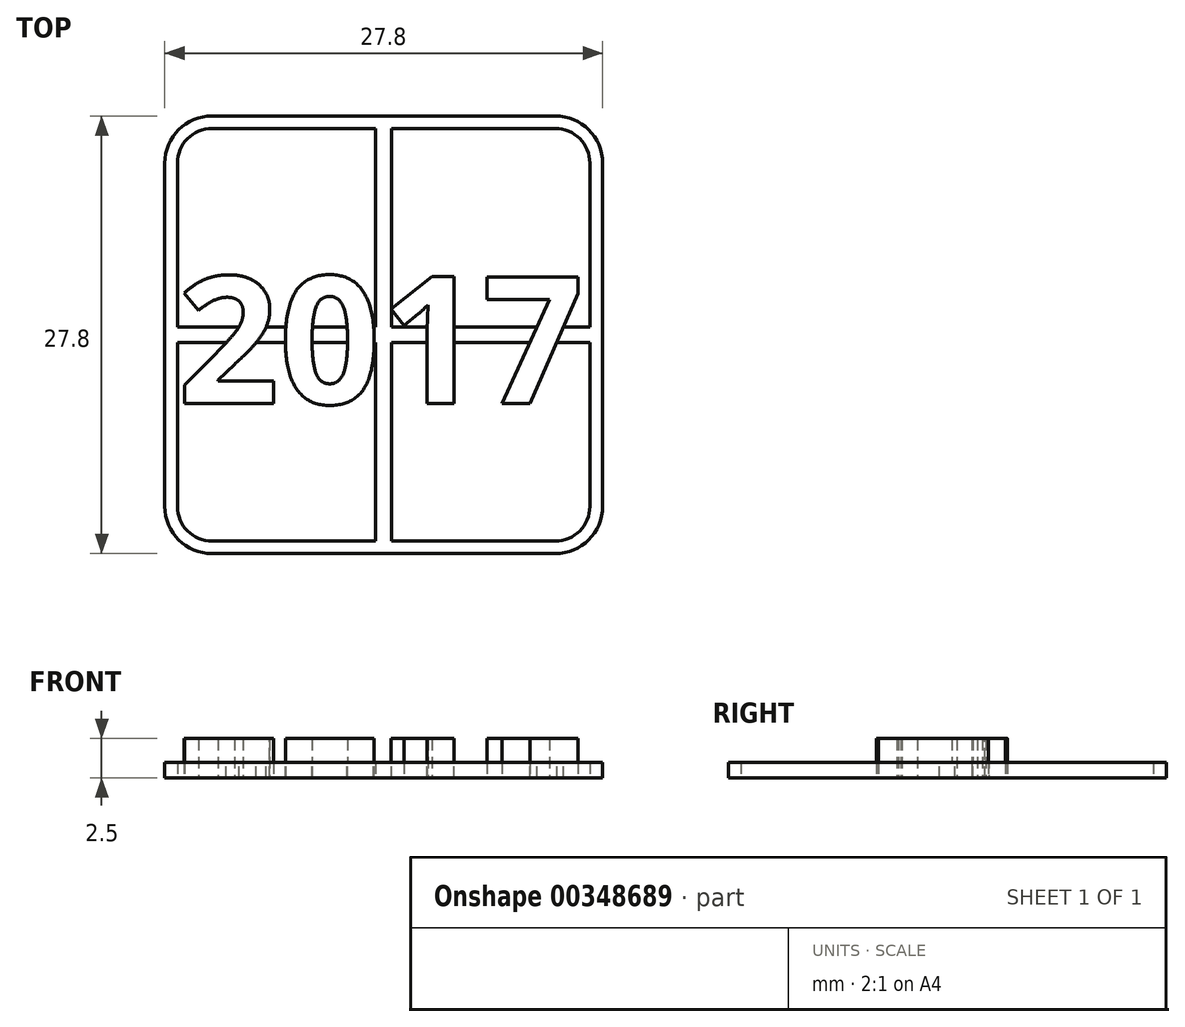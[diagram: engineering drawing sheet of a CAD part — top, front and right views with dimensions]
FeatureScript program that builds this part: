
annotation { "Feature Type Name" : "Feature", "Feature Type Description" : "" }
export const myFeature = defineFeature(function(context is Context, id is Id, definition is map)
    precondition{}
    {
        {
            var Q0;
            Q0=qCreatedBy(makeId("Top.planeOp"),FACE);
            var sketch = newSketch(context, id + "F0", { "sketchPlane" : qUnion([Q0])});
            skLineSegment(sketch, "E0", {"start": v(-13.9, 10.9) * mm, "end": v(-13.9, -10.9) * mm});
            skLineSegment(sketch, "E1", {"start": v(13.9, -10.9) * mm, "end": v(13.9, 10.9) * mm});
            skLineSegment(sketch, "E2", {"start": v(-10.9, 13.9) * mm, "end": v(10.9, 13.9) * mm});
            skLineSegment(sketch, "E3", {"start": v(-10.9, -13.9) * mm, "end": v(10.9, -13.9) * mm});
            skLineSegment(sketch, "E4", {"start": v(0, 13.9) * mm, "end": v(0, -13.9) * mm, "construction": true});
            skLineSegment(sketch, "E5", {"start": v(-13.9, 0) * mm, "end": v(13.9, 0) * mm, "construction": true});
            skPoint(sketch, "E6", {"position": v(0, 0) * mm});
            skPoint(sketch, "E7", {"position": v(0, 13.9) * mm});
            skPoint(sketch, "E8", {"position": v(0, -13.9) * mm});
            skPoint(sketch, "E9", {"position": v(-13.9, 0) * mm});
            skPoint(sketch, "E10", {"position": v(13.9, 0) * mm});
            skArc(sketch, "E11", {"start": v(-10.9, 13.9) * mm, "mid": v(-13.02, 13.02) * mm, "end": v(-13.9, 10.9) * mm});
            skArc(sketch, "E12", {"start": v(13.9, 10.9) * mm, "mid": v(13.02, 13.02) * mm, "end": v(10.9, 13.9) * mm});
            skArc(sketch, "E13", {"start": v(-13.9, -10.9) * mm, "mid": v(-13.02, -13.02) * mm, "end": v(-10.9, -13.9) * mm});
            skArc(sketch, "E14", {"start": v(10.9, -13.9) * mm, "mid": v(13.02, -13.02) * mm, "end": v(13.9, -10.9) * mm});
            skLineSegment(sketch, "E15", {"start": v(-0.5, 13.1) * mm, "end": v(-0.5, 0.5) * mm});
            skLineSegment(sketch, "E16", {"start": v(-0.5, 0.5) * mm, "end": v(-13.1, 0.5) * mm});
            skLineSegment(sketch, "E17", {"start": v(-13.1, 0.5) * mm, "end": v(-13.1, 10.9) * mm});
            skLineSegment(sketch, "E18", {"start": v(-0.5, 13.1) * mm, "end": v(-10.9, 13.1) * mm});
            skArc(sketch, "E19", {"start": v(-10.9, 13.1) * mm, "mid": v(-12.46, 12.46) * mm, "end": v(-13.1, 10.9) * mm});
            skLineSegment(sketch, "E20.MirrorCS", {"start": v(13.1, 0.5) * mm, "end": v(13.1, 10.9) * mm});
            skLineSegment(sketch, "E21.MirrorCS", {"start": v(0.5, 0.5) * mm, "end": v(13.1, 0.5) * mm});
            skLineSegment(sketch, "E22.MirrorCS", {"start": v(0.5, 13.1) * mm, "end": v(10.9, 13.1) * mm});
            skLineSegment(sketch, "E23.MirrorCS", {"start": v(0.5, 13.1) * mm, "end": v(0.5, 0.5) * mm});
            skArc(sketch, "E24.MirrorCS", {"start": v(10.9, 13.1) * mm, "mid": v(12.46, 12.46) * mm, "end": v(13.1, 10.9) * mm});
            skLineSegment(sketch, "E25.MirrorCS", {"start": v(0.5, -13.1) * mm, "end": v(10.9, -13.1) * mm});
            skLineSegment(sketch, "E26.MirrorCS", {"start": v(13.1, -0.5) * mm, "end": v(13.1, -10.9) * mm});
            skArc(sketch, "E27.MirrorCS", {"start": v(10.9, -13.1) * mm, "mid": v(12.46, -12.46) * mm, "end": v(13.1, -10.9) * mm});
            skLineSegment(sketch, "E28.MirrorCS", {"start": v(0.5, -13.1) * mm, "end": v(0.5, -0.5) * mm});
            skLineSegment(sketch, "E29.MirrorCS", {"start": v(0.5, -0.5) * mm, "end": v(13.1, -0.5) * mm});
            skLineSegment(sketch, "E30.MirrorCS", {"start": v(-0.5, -0.5) * mm, "end": v(-13.1, -0.5) * mm});
            skLineSegment(sketch, "E31.MirrorCS", {"start": v(-0.5, -13.1) * mm, "end": v(-0.5, -0.5) * mm});
            skLineSegment(sketch, "E32.MirrorCS", {"start": v(-0.5, -13.1) * mm, "end": v(-10.9, -13.1) * mm});
            skLineSegment(sketch, "E33.MirrorCS", {"start": v(-13.1, -0.5) * mm, "end": v(-13.1, -10.9) * mm});
            skArc(sketch, "E34.MirrorCS", {"start": v(-10.9, -13.1) * mm, "mid": v(-12.46, -12.46) * mm, "end": v(-13.1, -10.9) * mm});
            skSolve(sketch);
        }
        {
            var Q0;
            Q0=makeQuery(id+"F0.imprint","IMPRINT",FACE,{"disambiguationData":[TD([[makeQuery(id+"F0.imprint","IMPRINT",EDGE,{"derivedFrom":sQuery(id+"F0.wireOp",EDGE,"E0")}),1.0]])]});
            extrude(context, id + "F1", {"entities" : qUnion([Q0]), "depth" : 1 * mm});
        }
        {
            var Q0;
            Q0=makeQuery(id+"F1.opExtrude","CAP_FACE",FACE,{"disambiguationData":[OSD([sQuery(id+"F0.wireOp",EDGE,"E0"),sQuery(id+"F0.wireOp",EDGE,"E1"),sQuery(id+"F0.wireOp",EDGE,"E2"),sQuery(id+"F0.wireOp",EDGE,"E3"),sQuery(id+"F0.wireOp",EDGE,"E11"),sQuery(id+"F0.wireOp",EDGE,"E12"),sQuery(id+"F0.wireOp",EDGE,"E13"),sQuery(id+"F0.wireOp",EDGE,"E14"),sQuery(id+"F0.wireOp",EDGE,"E15"),sQuery(id+"F0.wireOp",EDGE,"E16"),sQuery(id+"F0.wireOp",EDGE,"E17"),sQuery(id+"F0.wireOp",EDGE,"E18"),sQuery(id+"F0.wireOp",EDGE,"E19"),sQuery(id+"F0.wireOp",EDGE,"E20.MirrorCS"),sQuery(id+"F0.wireOp",EDGE,"E21.MirrorCS"),sQuery(id+"F0.wireOp",EDGE,"E22.MirrorCS"),sQuery(id+"F0.wireOp",EDGE,"E23.MirrorCS"),sQuery(id+"F0.wireOp",EDGE,"E24.MirrorCS"),sQuery(id+"F0.wireOp",EDGE,"E25.MirrorCS"),sQuery(id+"F0.wireOp",EDGE,"E26.MirrorCS"),sQuery(id+"F0.wireOp",EDGE,"E27.MirrorCS"),sQuery(id+"F0.wireOp",EDGE,"E28.MirrorCS"),sQuery(id+"F0.wireOp",EDGE,"E29.MirrorCS"),sQuery(id+"F0.wireOp",EDGE,"E30.MirrorCS"),sQuery(id+"F0.wireOp",EDGE,"E31.MirrorCS"),sQuery(id+"F0.wireOp",EDGE,"E32.MirrorCS"),sQuery(id+"F0.wireOp",EDGE,"E33.MirrorCS"),sQuery(id+"F0.wireOp",EDGE,"E34.MirrorCS")])],"isStart":false});
            var sketch = newSketch(context, id + "F2", { "sketchPlane" : qUnion([Q0])});
            skText(sketch, "E35", { "text": "2017", "fontName": "OpenSans-Bold.ttf"});
            const initialGuessF2  = {"E35": [-0.0131, -0.00438, 1, 0, 0.00814]};
            skSetInitialGuess(sketch, initialGuessF2);
            skSolve(sketch);
        }
        {
            var Q0;
            Q0 = qSketchRegion(id + "F2", true);
            extrude(context, id + "F3", {"entities" : qUnion([Q0]), "operationType" : NewBodyOperationType.ADD, "depth" : 1.5 * mm});
        }
        {
            var Q0;
            {var subQ0=sQuery(id+"F2.wireOp",EDGE,"E35.sketch_text.stroke-50");var subQ2=sQuery(id+"F2.wireOp",EDGE,"E35.sketch_text.stroke-51");var subQ3=sQuery(id+"F2.wireOp",EDGE,"E35.sketch_text.stroke-52");var subQ4=sQuery(id+"F2.wireOp",EDGE,"E35.sketch_text.stroke-53");var subQ5=sQuery(id+"F2.wireOp",EDGE,"E35.sketch_text.stroke-54");var subQ6=sQuery(id+"F2.wireOp",EDGE,"E35.sketch_text.stroke-55");var subQ7=sQuery(id+"F2.wireOp",EDGE,"E35.sketch_text.stroke-56");var subQ8=sQuery(id+"F2.wireOp",EDGE,"E35.sketch_text.stroke-57");Q0=makeQuery(id+"F3.boolean.opBoolean","SPLIT",FACE,{"disambiguationData":[TD([makeQuery(id+"F3.opExtrude","SWEPT_FACE",FACE,{"disambiguationData":[OSD([subQ2])]})])],"derivedFrom":makeQuery(id+"F3.opExtrude","CAP_FACE",FACE,{"disambiguationData":[OSD([subQ0,subQ2,subQ3,subQ4,subQ5,subQ6,subQ7,subQ8,sQuery(id+"F2.wireOp",EDGE,"E35.sketch_text.stroke-58"),sQuery(id+"F2.wireOp",EDGE,"E35.sketch_text.stroke-59"),sQuery(id+"F2.wireOp",EDGE,"E35.sketch_text.stroke-60"),sQuery(id+"F2.wireOp",EDGE,"E35.sketch_text.stroke-61"),sQuery(id+"F2.wireOp",EDGE,"E35.sketch_text.stroke-62"),sQuery(id+"F2.wireOp",EDGE,"E35.sketch_text.stroke-63"),sQuery(id+"F2.wireOp",EDGE,"E35.sketch_text.stroke-64"),sQuery(id+"F2.wireOp",EDGE,"E35.sketch_text.stroke-65"),sQuery(id+"F2.wireOp",EDGE,"E35.sketch_text.stroke-66"),sQuery(id+"F2.wireOp",EDGE,"E35.sketch_text.stroke-67"),sQuery(id+"F2.wireOp",EDGE,"E35.sketch_text.stroke-68"),sQuery(id+"F2.wireOp",EDGE,"E35.sketch_text.stroke-69"),sQuery(id+"F2.wireOp",EDGE,"E35.sketch_text.stroke-70"),sQuery(id+"F2.wireOp",EDGE,"E35.sketch_text.stroke-71"),sQuery(id+"F2.wireOp",EDGE,"E35.sketch_text.stroke-72"),sQuery(id+"F2.wireOp",EDGE,"E35.sketch_text.stroke-73"),sQuery(id+"F2.wireOp",EDGE,"E35.sketch_text.stroke-74")])],"isStart":true})});}
            var Q1;
            {var subQ0=sQuery(id+"F2.wireOp",EDGE,"E35.sketch_text.stroke-67");var subQ1=sQuery(id+"F2.wireOp",EDGE,"E35.sketch_text.stroke-66");var subQ2=sQuery(id+"F2.wireOp",EDGE,"E35.sketch_text.stroke-65");var subQ3=sQuery(id+"F2.wireOp",EDGE,"E35.sketch_text.stroke-64");var subQ4=sQuery(id+"F2.wireOp",EDGE,"E35.sketch_text.stroke-63");var subQ5=sQuery(id+"F2.wireOp",EDGE,"E35.sketch_text.stroke-62");var subQ6=sQuery(id+"F2.wireOp",EDGE,"E35.sketch_text.stroke-61");var subQ7=sQuery(id+"F0.wireOp",EDGE,"E29.MirrorCS");var subQ8=sQuery(id+"F2.wireOp",EDGE,"E35.sketch_text.stroke-50");var subQ9=sQuery(id+"F2.wireOp",EDGE,"E35.sketch_text.stroke-71");var subQ10=sQuery(id+"F2.wireOp",EDGE,"E35.sketch_text.stroke-68");var subQ11=sQuery(id+"F2.wireOp",EDGE,"E35.sketch_text.stroke-69");var subQ12=sQuery(id+"F2.wireOp",EDGE,"E35.sketch_text.stroke-70");var subQ13=sQuery(id+"F2.wireOp",EDGE,"E35.sketch_text.stroke-72");var subQ14=sQuery(id+"F2.wireOp",EDGE,"E35.sketch_text.stroke-73");var subQ15=sQuery(id+"F2.wireOp",EDGE,"E35.sketch_text.stroke-74");Q1=makeQuery(id+"F3.boolean.opBoolean","SPLIT",FACE,{"disambiguationData":[TD([makeQuery(id+"F1.opExtrude","SWEPT_FACE",FACE,{"disambiguationData":[OSD([subQ7])]})])],"derivedFrom":makeQuery(id+"F3.opExtrude","CAP_FACE",FACE,{"disambiguationData":[OSD([subQ8,sQuery(id+"F2.wireOp",EDGE,"E35.sketch_text.stroke-51"),sQuery(id+"F2.wireOp",EDGE,"E35.sketch_text.stroke-52"),sQuery(id+"F2.wireOp",EDGE,"E35.sketch_text.stroke-53"),sQuery(id+"F2.wireOp",EDGE,"E35.sketch_text.stroke-54"),sQuery(id+"F2.wireOp",EDGE,"E35.sketch_text.stroke-55"),sQuery(id+"F2.wireOp",EDGE,"E35.sketch_text.stroke-56"),sQuery(id+"F2.wireOp",EDGE,"E35.sketch_text.stroke-57"),sQuery(id+"F2.wireOp",EDGE,"E35.sketch_text.stroke-58"),sQuery(id+"F2.wireOp",EDGE,"E35.sketch_text.stroke-59"),sQuery(id+"F2.wireOp",EDGE,"E35.sketch_text.stroke-60"),subQ6,subQ5,subQ4,subQ3,subQ2,subQ1,subQ0,subQ10,subQ11,subQ12,subQ9,subQ13,subQ14,subQ15])],"isStart":true})});}
            var Q2;
            {var subQ1=sQuery(id+"F2.wireOp",EDGE,"E35.sketch_text.stroke-60");var subQ2=sQuery(id+"F2.wireOp",EDGE,"E35.sketch_text.stroke-59");Q2=makeQuery(id+"F3.boolean.opBoolean","SPLIT",FACE,{"disambiguationData":[TD([makeQuery(id+"F3.opExtrude","SWEPT_FACE",FACE,{"disambiguationData":[OSD([subQ2])]})])],"derivedFrom":makeQuery(id+"F3.opExtrude","CAP_FACE",FACE,{"disambiguationData":[OSD([sQuery(id+"F2.wireOp",EDGE,"E35.sketch_text.stroke-50"),sQuery(id+"F2.wireOp",EDGE,"E35.sketch_text.stroke-51"),sQuery(id+"F2.wireOp",EDGE,"E35.sketch_text.stroke-52"),sQuery(id+"F2.wireOp",EDGE,"E35.sketch_text.stroke-53"),sQuery(id+"F2.wireOp",EDGE,"E35.sketch_text.stroke-54"),sQuery(id+"F2.wireOp",EDGE,"E35.sketch_text.stroke-55"),sQuery(id+"F2.wireOp",EDGE,"E35.sketch_text.stroke-56"),sQuery(id+"F2.wireOp",EDGE,"E35.sketch_text.stroke-57"),sQuery(id+"F2.wireOp",EDGE,"E35.sketch_text.stroke-58"),subQ2,subQ1,sQuery(id+"F2.wireOp",EDGE,"E35.sketch_text.stroke-61"),sQuery(id+"F2.wireOp",EDGE,"E35.sketch_text.stroke-62"),sQuery(id+"F2.wireOp",EDGE,"E35.sketch_text.stroke-63"),sQuery(id+"F2.wireOp",EDGE,"E35.sketch_text.stroke-64"),sQuery(id+"F2.wireOp",EDGE,"E35.sketch_text.stroke-65"),sQuery(id+"F2.wireOp",EDGE,"E35.sketch_text.stroke-66"),sQuery(id+"F2.wireOp",EDGE,"E35.sketch_text.stroke-67"),sQuery(id+"F2.wireOp",EDGE,"E35.sketch_text.stroke-68"),sQuery(id+"F2.wireOp",EDGE,"E35.sketch_text.stroke-69"),sQuery(id+"F2.wireOp",EDGE,"E35.sketch_text.stroke-70"),sQuery(id+"F2.wireOp",EDGE,"E35.sketch_text.stroke-71"),sQuery(id+"F2.wireOp",EDGE,"E35.sketch_text.stroke-72"),sQuery(id+"F2.wireOp",EDGE,"E35.sketch_text.stroke-73"),sQuery(id+"F2.wireOp",EDGE,"E35.sketch_text.stroke-74")])],"isStart":true})});}
            var Q3;
            {var subQ0=sQuery(id+"F2.wireOp",EDGE,"E35.sketch_text.stroke-48");var subQ1=sQuery(id+"F2.wireOp",EDGE,"E35.sketch_text.stroke-47");var subQ2=sQuery(id+"F2.wireOp",EDGE,"E35.sketch_text.stroke-46");var subQ3=sQuery(id+"F2.wireOp",EDGE,"E35.sketch_text.stroke-45");var subQ4=sQuery(id+"F2.wireOp",EDGE,"E35.sketch_text.stroke-43");var subQ6=sQuery(id+"F0.wireOp",EDGE,"E21.MirrorCS");var subQ7=sQuery(id+"F2.wireOp",EDGE,"E35.sketch_text.stroke-42");var subQ8=sQuery(id+"F2.wireOp",EDGE,"E35.sketch_text.stroke-44");var subQ9=sQuery(id+"F2.wireOp",EDGE,"E35.sketch_text.stroke-49");Q3=makeQuery(id+"F3.boolean.opBoolean","SPLIT",FACE,{"disambiguationData":[TD([makeQuery(id+"F1.opExtrude","SWEPT_FACE",FACE,{"disambiguationData":[OSD([subQ6])]})])],"derivedFrom":makeQuery(id+"F3.opExtrude","CAP_FACE",FACE,{"disambiguationData":[OSD([sQuery(id+"F2.wireOp",EDGE,"E35.sketch_text.stroke-40"),sQuery(id+"F2.wireOp",EDGE,"E35.sketch_text.stroke-41"),subQ7,subQ4,subQ8,subQ3,subQ2,subQ1,subQ0,subQ9])],"isStart":true})});}
            var Q4;
            {var subQ0=sQuery(id+"F2.wireOp",EDGE,"E35.sketch_text.stroke-41");var subQ1=sQuery(id+"F0.wireOp",EDGE,"E29.MirrorCS");var subQ2=sQuery(id+"F2.wireOp",EDGE,"E35.sketch_text.stroke-40");var subQ3=sQuery(id+"F2.wireOp",EDGE,"E35.sketch_text.stroke-49");Q4=makeQuery(id+"F3.boolean.opBoolean","SPLIT",FACE,{"disambiguationData":[TD([makeQuery(id+"F1.opExtrude","SWEPT_FACE",FACE,{"disambiguationData":[OSD([subQ1])]})])],"derivedFrom":makeQuery(id+"F3.opExtrude","CAP_FACE",FACE,{"disambiguationData":[OSD([subQ2,subQ0,sQuery(id+"F2.wireOp",EDGE,"E35.sketch_text.stroke-42"),sQuery(id+"F2.wireOp",EDGE,"E35.sketch_text.stroke-43"),sQuery(id+"F2.wireOp",EDGE,"E35.sketch_text.stroke-44"),sQuery(id+"F2.wireOp",EDGE,"E35.sketch_text.stroke-45"),sQuery(id+"F2.wireOp",EDGE,"E35.sketch_text.stroke-46"),sQuery(id+"F2.wireOp",EDGE,"E35.sketch_text.stroke-47"),sQuery(id+"F2.wireOp",EDGE,"E35.sketch_text.stroke-48"),subQ3])],"isStart":true})});}
            var Q5;
            {var subQ0=sQuery(id+"F2.wireOp",EDGE,"E35.sketch_text.stroke-28");var subQ1=sQuery(id+"F0.wireOp",EDGE,"E16");var subQ2=sQuery(id+"F2.wireOp",EDGE,"E35.sketch_text.stroke-39");var subQ3=sQuery(id+"F2.wireOp",EDGE,"E35.sketch_text.stroke-29");var subQ4=sQuery(id+"F2.wireOp",EDGE,"E35.sketch_text.stroke-30");var subQ5=sQuery(id+"F2.wireOp",EDGE,"E35.sketch_text.stroke-31");var subQ6=sQuery(id+"F2.wireOp",EDGE,"E35.sketch_text.stroke-36");var subQ7=sQuery(id+"F2.wireOp",EDGE,"E35.sketch_text.stroke-37");var subQ8=sQuery(id+"F2.wireOp",EDGE,"E35.sketch_text.stroke-38");Q5=makeQuery(id+"F3.boolean.opBoolean","SPLIT",FACE,{"disambiguationData":[TD([makeQuery(id+"F1.opExtrude","SWEPT_FACE",FACE,{"disambiguationData":[OSD([subQ1])]})])],"derivedFrom":makeQuery(id+"F3.opExtrude","CAP_FACE",FACE,{"disambiguationData":[OSD([sQuery(id+"F2.wireOp",EDGE,"E35.sketch_text.stroke-24"),sQuery(id+"F2.wireOp",EDGE,"E35.sketch_text.stroke-25"),sQuery(id+"F2.wireOp",EDGE,"E35.sketch_text.stroke-26"),sQuery(id+"F2.wireOp",EDGE,"E35.sketch_text.stroke-27"),subQ0,subQ3,subQ4,subQ5,sQuery(id+"F2.wireOp",EDGE,"E35.sketch_text.stroke-32"),sQuery(id+"F2.wireOp",EDGE,"E35.sketch_text.stroke-33"),sQuery(id+"F2.wireOp",EDGE,"E35.sketch_text.stroke-34"),sQuery(id+"F2.wireOp",EDGE,"E35.sketch_text.stroke-35"),subQ6,subQ7,subQ8,subQ2])],"isStart":true})});}
            var Q6;
            {var subQ0=sQuery(id+"F2.wireOp",EDGE,"E35.sketch_text.stroke-24");var subQ1=sQuery(id+"F2.wireOp",EDGE,"E35.sketch_text.stroke-33");var subQ2=sQuery(id+"F0.wireOp",EDGE,"E30.MirrorCS");var subQ3=sQuery(id+"F2.wireOp",EDGE,"E35.sketch_text.stroke-25");var subQ4=sQuery(id+"F2.wireOp",EDGE,"E35.sketch_text.stroke-26");var subQ5=sQuery(id+"F2.wireOp",EDGE,"E35.sketch_text.stroke-27");var subQ6=sQuery(id+"F2.wireOp",EDGE,"E35.sketch_text.stroke-32");var subQ7=sQuery(id+"F2.wireOp",EDGE,"E35.sketch_text.stroke-34");var subQ8=sQuery(id+"F2.wireOp",EDGE,"E35.sketch_text.stroke-35");Q6=makeQuery(id+"F3.boolean.opBoolean","SPLIT",FACE,{"disambiguationData":[TD([makeQuery(id+"F1.opExtrude","SWEPT_FACE",FACE,{"disambiguationData":[OSD([subQ2])]})])],"derivedFrom":makeQuery(id+"F3.opExtrude","CAP_FACE",FACE,{"disambiguationData":[OSD([subQ0,subQ3,subQ4,subQ5,sQuery(id+"F2.wireOp",EDGE,"E35.sketch_text.stroke-28"),sQuery(id+"F2.wireOp",EDGE,"E35.sketch_text.stroke-29"),sQuery(id+"F2.wireOp",EDGE,"E35.sketch_text.stroke-30"),sQuery(id+"F2.wireOp",EDGE,"E35.sketch_text.stroke-31"),subQ6,subQ1,subQ7,subQ8,sQuery(id+"F2.wireOp",EDGE,"E35.sketch_text.stroke-36"),sQuery(id+"F2.wireOp",EDGE,"E35.sketch_text.stroke-37"),sQuery(id+"F2.wireOp",EDGE,"E35.sketch_text.stroke-38"),sQuery(id+"F2.wireOp",EDGE,"E35.sketch_text.stroke-39")])],"isStart":true})});}
            var Q7;
            {var subQ0=sQuery(id+"F2.wireOp",EDGE,"E35.sketch_text.stroke-11");var subQ1=sQuery(id+"F2.wireOp",EDGE,"E35.sketch_text.stroke-9");var subQ2=sQuery(id+"F2.wireOp",EDGE,"E35.sketch_text.stroke-7");var subQ3=sQuery(id+"F2.wireOp",EDGE,"E35.sketch_text.stroke-6");var subQ4=sQuery(id+"F2.wireOp",EDGE,"E35.sketch_text.stroke-10");var subQ5=sQuery(id+"F0.wireOp",EDGE,"E16");var subQ6=sQuery(id+"F2.wireOp",EDGE,"E35.sketch_text.stroke-8");var subQ7=sQuery(id+"F2.wireOp",EDGE,"E35.sketch_text.stroke-5");var subQ8=sQuery(id+"F2.wireOp",EDGE,"E35.sketch_text.stroke-4");var subQ9=sQuery(id+"F2.wireOp",EDGE,"E35.sketch_text.stroke-12");var subQ10=sQuery(id+"F2.wireOp",EDGE,"E35.sketch_text.stroke-13");var subQ11=sQuery(id+"F2.wireOp",EDGE,"E35.sketch_text.stroke-14");var subQ12=sQuery(id+"F2.wireOp",EDGE,"E35.sketch_text.stroke-15");var subQ13=sQuery(id+"F2.wireOp",EDGE,"E35.sketch_text.stroke-16");var subQ14=sQuery(id+"F2.wireOp",EDGE,"E35.sketch_text.stroke-17");var subQ15=sQuery(id+"F2.wireOp",EDGE,"E35.sketch_text.stroke-18");Q7=makeQuery(id+"F3.boolean.opBoolean","SPLIT",FACE,{"disambiguationData":[TD([makeQuery(id+"F1.opExtrude","SWEPT_FACE",FACE,{"disambiguationData":[OSD([subQ5])]})])],"derivedFrom":makeQuery(id+"F3.opExtrude","CAP_FACE",FACE,{"disambiguationData":[OSD([sQuery(id+"F2.wireOp",EDGE,"E35.sketch_text.stroke-0"),sQuery(id+"F2.wireOp",EDGE,"E35.sketch_text.stroke-1"),sQuery(id+"F2.wireOp",EDGE,"E35.sketch_text.stroke-2"),sQuery(id+"F2.wireOp",EDGE,"E35.sketch_text.stroke-3"),subQ8,subQ7,subQ3,subQ2,subQ6,subQ1,subQ4,subQ0,subQ9,subQ10,subQ11,subQ12,subQ13,subQ14,subQ15,sQuery(id+"F2.wireOp",EDGE,"E35.sketch_text.stroke-19"),sQuery(id+"F2.wireOp",EDGE,"E35.sketch_text.stroke-20"),sQuery(id+"F2.wireOp",EDGE,"E35.sketch_text.stroke-21"),sQuery(id+"F2.wireOp",EDGE,"E35.sketch_text.stroke-22"),sQuery(id+"F2.wireOp",EDGE,"E35.sketch_text.stroke-23")])],"isStart":true})});}
            var Q8;
            {var subQ0=sQuery(id+"F2.wireOp",EDGE,"E35.sketch_text.stroke-19");var subQ1=sQuery(id+"F0.wireOp",EDGE,"E30.MirrorCS");var subQ2=sQuery(id+"F2.wireOp",EDGE,"E35.sketch_text.stroke-3");var subQ3=sQuery(id+"F2.wireOp",EDGE,"E35.sketch_text.stroke-2");var subQ4=sQuery(id+"F2.wireOp",EDGE,"E35.sketch_text.stroke-21");var subQ5=sQuery(id+"F2.wireOp",EDGE,"E35.sketch_text.stroke-0");var subQ6=sQuery(id+"F2.wireOp",EDGE,"E35.sketch_text.stroke-22");var subQ7=sQuery(id+"F2.wireOp",EDGE,"E35.sketch_text.stroke-20");var subQ8=sQuery(id+"F2.wireOp",EDGE,"E35.sketch_text.stroke-1");var subQ9=sQuery(id+"F2.wireOp",EDGE,"E35.sketch_text.stroke-23");Q8=makeQuery(id+"F3.boolean.opBoolean","SPLIT",FACE,{"disambiguationData":[TD([makeQuery(id+"F1.opExtrude","SWEPT_FACE",FACE,{"disambiguationData":[OSD([subQ1])]})])],"derivedFrom":makeQuery(id+"F3.opExtrude","CAP_FACE",FACE,{"disambiguationData":[OSD([subQ5,subQ8,subQ3,subQ2,sQuery(id+"F2.wireOp",EDGE,"E35.sketch_text.stroke-4"),sQuery(id+"F2.wireOp",EDGE,"E35.sketch_text.stroke-5"),sQuery(id+"F2.wireOp",EDGE,"E35.sketch_text.stroke-6"),sQuery(id+"F2.wireOp",EDGE,"E35.sketch_text.stroke-7"),sQuery(id+"F2.wireOp",EDGE,"E35.sketch_text.stroke-8"),sQuery(id+"F2.wireOp",EDGE,"E35.sketch_text.stroke-9"),sQuery(id+"F2.wireOp",EDGE,"E35.sketch_text.stroke-10"),sQuery(id+"F2.wireOp",EDGE,"E35.sketch_text.stroke-11"),sQuery(id+"F2.wireOp",EDGE,"E35.sketch_text.stroke-12"),sQuery(id+"F2.wireOp",EDGE,"E35.sketch_text.stroke-13"),sQuery(id+"F2.wireOp",EDGE,"E35.sketch_text.stroke-14"),sQuery(id+"F2.wireOp",EDGE,"E35.sketch_text.stroke-15"),sQuery(id+"F2.wireOp",EDGE,"E35.sketch_text.stroke-16"),sQuery(id+"F2.wireOp",EDGE,"E35.sketch_text.stroke-17"),sQuery(id+"F2.wireOp",EDGE,"E35.sketch_text.stroke-18"),subQ0,subQ7,subQ4,subQ6,subQ9])],"isStart":true})});}
            extrude(context, id + "F4", {"entities" : qUnion([Q0, Q1, Q2, Q3, Q4, Q5, Q6, Q7, Q8]), "operationType" : NewBodyOperationType.ADD, "depth" : 1 * mm});
        }
    });
